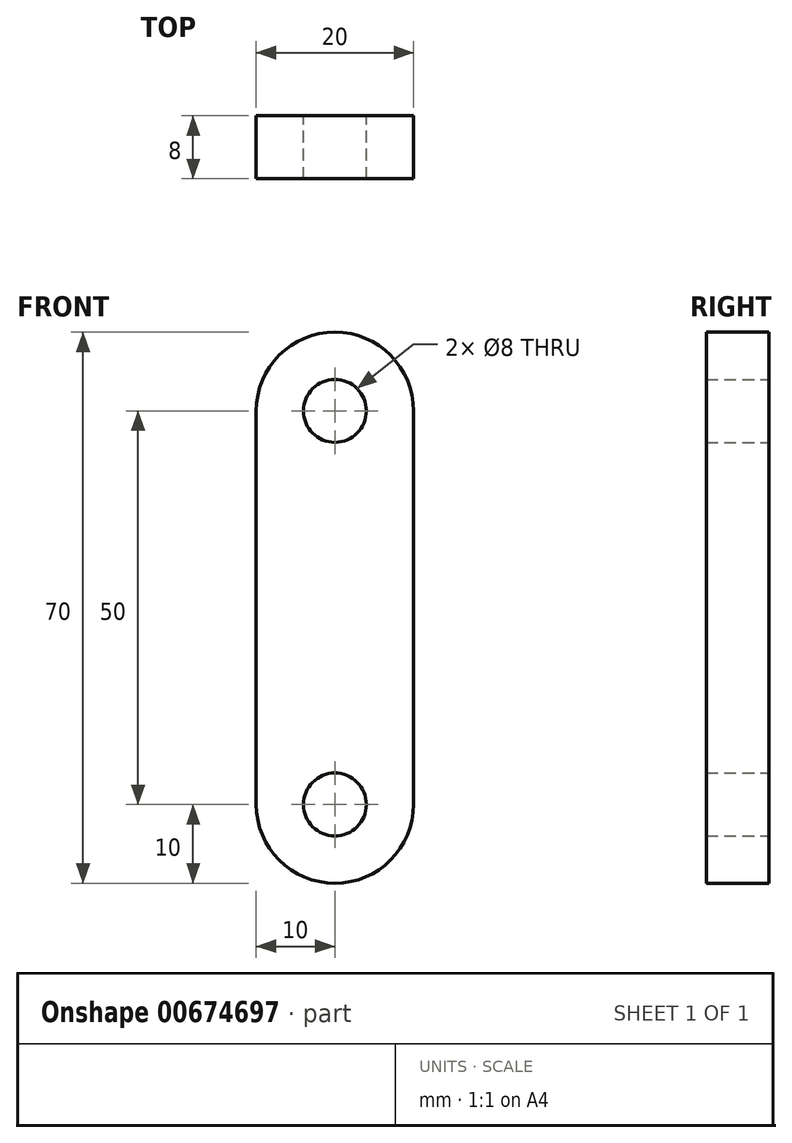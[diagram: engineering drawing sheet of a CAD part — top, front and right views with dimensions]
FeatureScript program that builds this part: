
annotation { "Feature Type Name" : "Feature", "Feature Type Description" : "" }
export const myFeature = defineFeature(function(context is Context, id is Id, definition is map)
    precondition{}
    {
        {
            var Q0;
            Q0=qCreatedBy(makeId("Front.planeOp"),FACE);
            var sketch = newSketch(context, id + "F0", { "sketchPlane" : qUnion([Q0])});
            skArc(sketch, "E0", {"start": v(-10, 0) * mm, "mid": v(0, -10) * mm, "end": v(10, 0) * mm});
            skArc(sketch, "E1", {"start": v(10, 50) * mm, "mid": v(0, 60) * mm, "end": v(-10, 50) * mm});
            skCircle(sketch, "E2", {"center": v(0, 50) * mm, "radius": 4 * mm});
            skCircle(sketch, "E3", {"center": v(0, 0) * mm, "radius": 4 * mm});
            skLineSegment(sketch, "E4", {"start": v(-10, 50) * mm, "end": v(-10, 0) * mm});
            skLineSegment(sketch, "E5", {"start": v(10, 50) * mm, "end": v(10, 0) * mm});
            skSolve(sketch);
        }
        {
            var Q0;
            Q0 = qSketchRegion(id + "F0", true);
            extrude(context, id + "F1", {"entities" : qUnion([Q0]), "depth" : 8 * mm, "offsetDistance" : 25 * mm});
        }
    });
